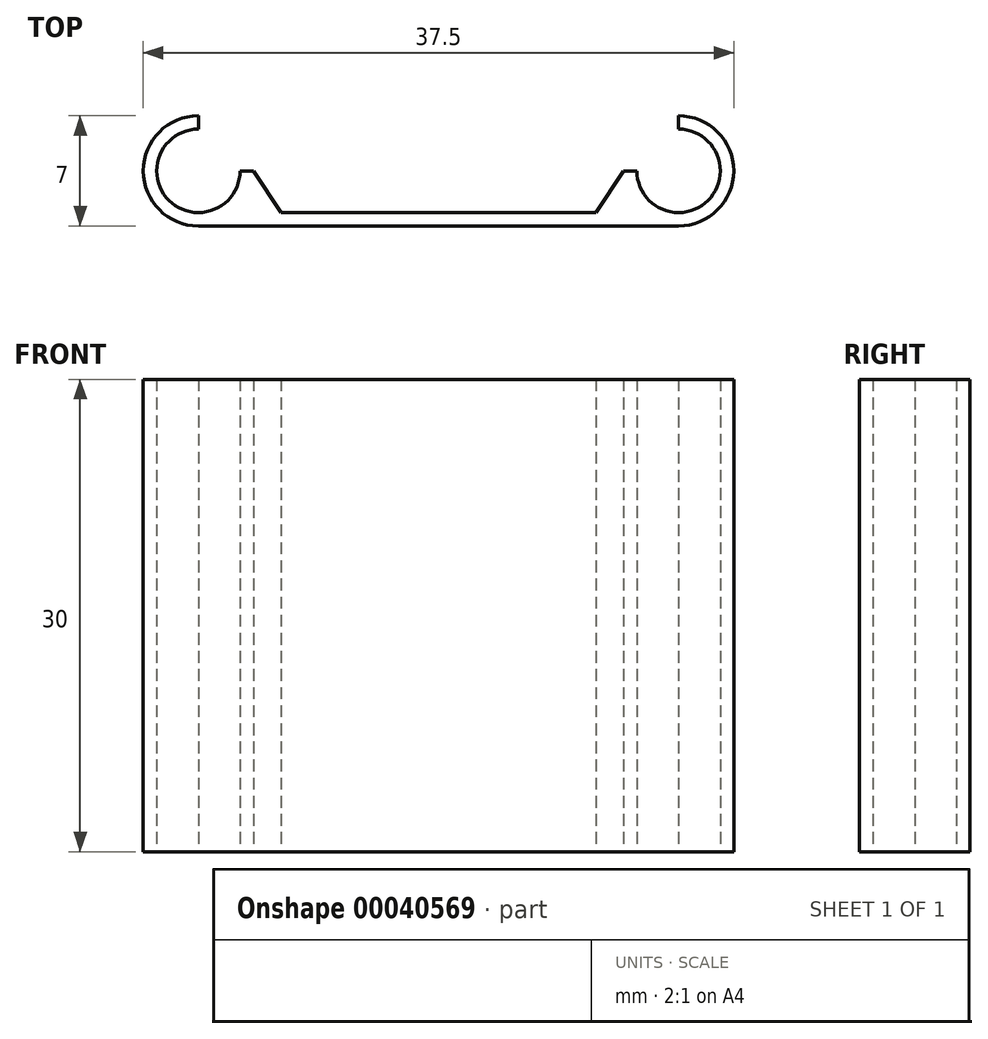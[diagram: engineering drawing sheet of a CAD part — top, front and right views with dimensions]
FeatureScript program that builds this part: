
annotation { "Feature Type Name" : "Feature", "Feature Type Description" : "" }
export const myFeature = defineFeature(function(context is Context, id is Id, definition is map)
    precondition{}
    {
        {
            var Q0;
            Q0=qCreatedBy(makeId("Top.planeOp"),FACE);
            var sketch = newSketch(context, id + "F0", { "sketchPlane" : qUnion([Q0])});
            skArc(sketch, "E0", {"start": v(-2.65, 0) * mm, "mid": v(1.87, -1.87) * mm, "end": v(0, 2.65) * mm});
            skArc(sketch, "E1", {"start": v(-30.5, 2.65) * mm, "mid": v(-32.37, -1.87) * mm, "end": v(-27.85, 0) * mm});
            skLineSegment(sketch, "E2", {"start": v(0, -3.5) * mm, "end": v(-30.5, -3.5) * mm});
            skArc(sketch, "E3", {"start": v(-30.5, 3.5) * mm, "mid": v(-32.97, -2.47) * mm, "end": v(-27, 0) * mm});
            skArc(sketch, "E4", {"start": v(-3.5, 0) * mm, "mid": v(2.47, -2.47) * mm, "end": v(0, 3.5) * mm});
            skLineSegment(sketch, "E5", {"start": v(0, -2.65) * mm, "end": v(-30.5, -2.65) * mm});
            skLineSegment(sketch, "E6", {"start": v(-27, 0) * mm, "end": v(-25.25, -2.65) * mm});
            skLineSegment(sketch, "E7", {"start": v(-3.5, 0) * mm, "end": v(-5.25, -2.65) * mm});
            skLineSegment(sketch, "E8", {"start": v(-30.5, 3.5) * mm, "end": v(-30.5, 2.65) * mm});
            skLineSegment(sketch, "E9", {"start": v(-27, 0) * mm, "end": v(-27.85, 0) * mm});
            skLineSegment(sketch, "E10", {"start": v(-3.5, 0) * mm, "end": v(-2.65, 0) * mm});
            skLineSegment(sketch, "E11", {"start": v(0, 2.65) * mm, "end": v(0, 3.5) * mm});
            skSolve(sketch);
        }
        {
            var Q0;
            Q0 = qSketchRegion(id + "F0", true);
            extrude(context, id + "F1", {"entities" : qUnion([Q0]), "depth" : 30 * mm});
        }
    });
